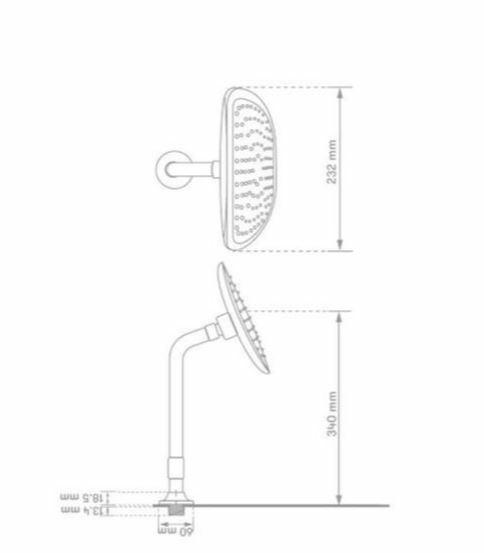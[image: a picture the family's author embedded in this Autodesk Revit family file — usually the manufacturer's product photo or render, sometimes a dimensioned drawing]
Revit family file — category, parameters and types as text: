
# Revit family: BL-1430-11-REGADERA GENISIS
name_source: partatom
category: Plumbing Fixtures
revit_build: Autodesk Revit 2018 (Build: 20170223_1515(x64)
units: mm (PartAtom-declared; Revit-internal decimal feet)

## family parameters
Cut with Voids When Loaded = No
Host = Face
OmniClass Number = 23.31.11.00
Part Type = Normal
Room Calculation Point = No
Round Connector Dimension = Use Diameter
Shared = No

## types (1)
- BL-1430-11
    Alto = 100 mm  [stored 0.328084 ft]
    Ancho = 90 mm  [stored 0.295276 ft]
    CW Connection = Yes
    Default Elevation = 0 mm  [stored 0 ft]
    Description = Regadera
    HW Connection = Yes
    Link Ficha Tecnica = https://infotecnica.gricol.com
    Manufacturer = Gricol
    Model = BL-1430-11
    Plastico ABS Cromado = Plastico ABS Cromado
    Product Name = REGADERA GENESIS I
    Profundidad = 165 mm
    Type Image = REGADERA GENESIS FOTO.JPG
    URL = https://www.gricol.com
    Vent Connection = No
    Waste Connection = No

note: [stored X ft] marks values corroborated as IEEE doubles in the binary element streams (Revit-internal decimal feet)

## geometry (parser evidence)
native form markers: Blend x4, Sweep x5
no freeform markers — native parametric forms only
